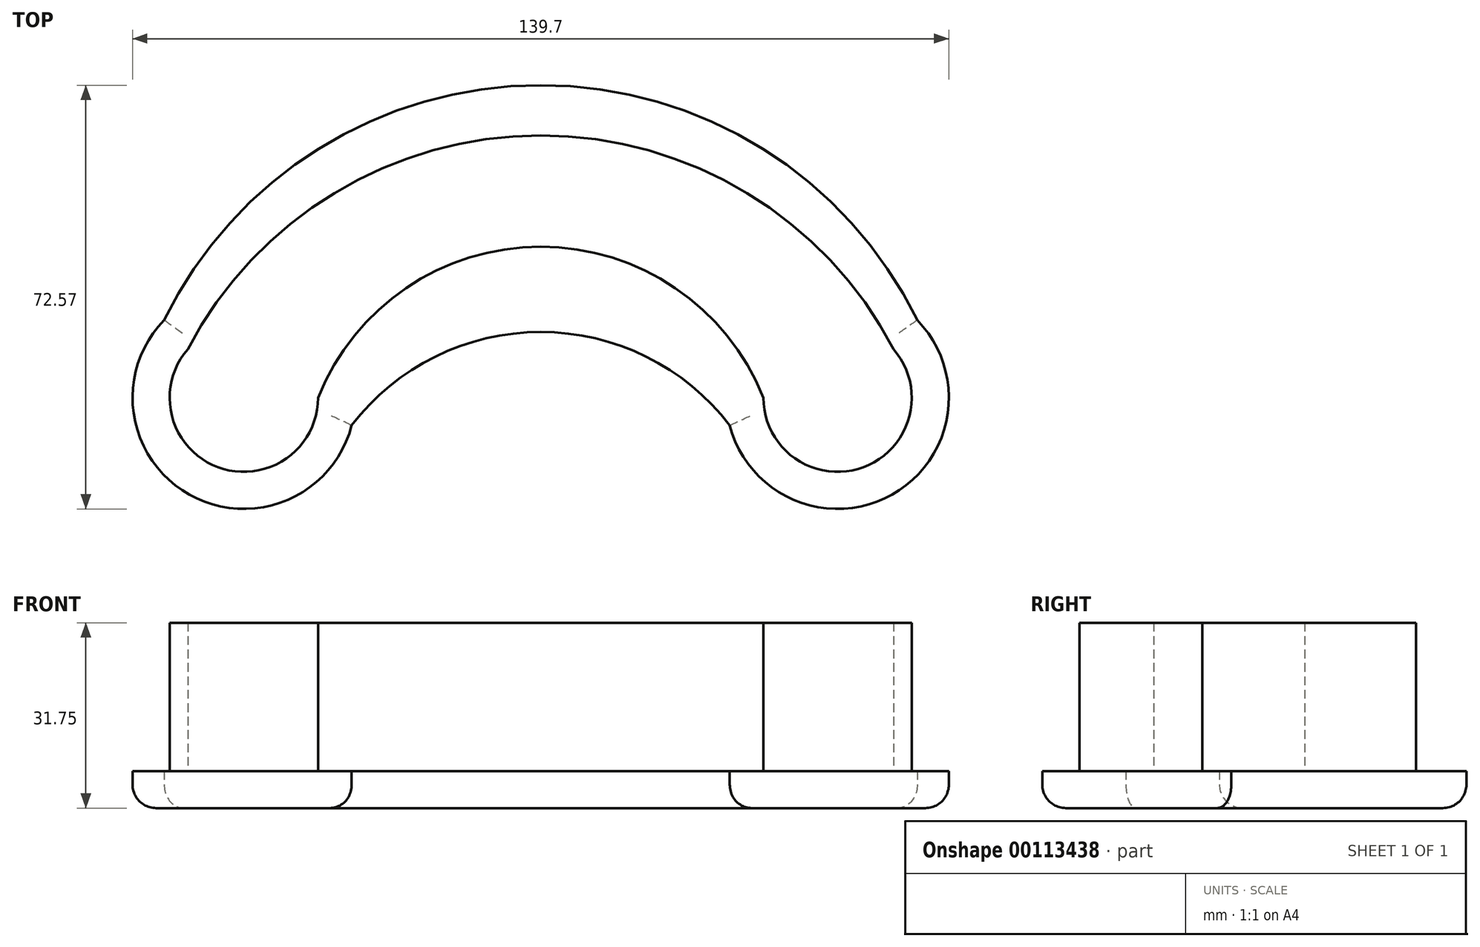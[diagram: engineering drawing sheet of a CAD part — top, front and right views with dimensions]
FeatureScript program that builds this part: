
annotation { "Feature Type Name" : "Feature", "Feature Type Description" : "" }
export const myFeature = defineFeature(function(context is Context, id is Id, definition is map)
    precondition{}
    {
        {
            var Q0;
            Q0=qCreatedBy(makeId("Top.planeOp"),FACE);
            var sketch = newSketch(context, id + "F0", { "sketchPlane" : qUnion([Q0])});
            skCircle(sketch, "E0", {"center": v(-44.09, 19.27) * mm, "radius": 19.05 * mm});
            skCircle(sketch, "E1", {"center": v(57.51, 19.27) * mm, "radius": 19.05 * mm});
            skLineSegment(sketch, "E2", {"start": v(-44.09, 19.27) * mm, "end": v(57.51, 19.27) * mm});
            skLineSegment(sketch, "E3", {"start": v(-57.73, 32.57) * mm, "end": v(71.15, 32.57) * mm});
            skLineSegment(sketch, "E4", {"start": v(-25.64, 14.52) * mm, "end": v(39.06, 14.52) * mm});
            skArc(sketch, "E5", {"start": v(71.15, 32.57) * mm, "mid": v(6.71, 72.8) * mm, "end": v(-57.73, 32.57) * mm});
            skArc(sketch, "E6", {"start": v(39.06, 14.52) * mm, "mid": v(6.71, 30.53) * mm, "end": v(-25.64, 14.52) * mm});
            skSolve(sketch);
        }
        {
            var Q0;
            {var subQ0=sQuery(id+"F0.wireOp",EDGE,"E0");var subQ1=makeQuery(id+"F0.imprint","INTERSECT",VERTEX,{"derivedFrom":[subQ0,sQuery(id+"F0.wireOp",EDGE,"E2")]});Q0=makeQuery(id+"F0.imprint","IMPRINT",FACE,{"disambiguationData":[TD([[makeQuery(id+"F0.imprint","IMPRINT",EDGE,{"disambiguationData":[TD([[subQ1,-1.0]])],"derivedFrom":subQ0}),1.0]])]});}
            var Q1;
            {var subQ0=sQuery(id+"F0.wireOp",EDGE,"cqztKuuP-2mC5-SIxx-0093-MniZhsKi1Iyt");var subQ1=sQuery(id+"F0.wireOp",EDGE,"E0");var subQ2=makeQuery(id+"F0.imprint","INTERSECT",VERTEX,{"derivedFrom":[subQ1,subQ0]});Q1=makeQuery(id+"F0.imprint","IMPRINT",FACE,{"disambiguationData":[TD([[makeQuery(id+"F0.imprint","IMPRINT",EDGE,{"disambiguationData":[TD([[subQ2,1.0]])],"derivedFrom":subQ1}),1.0]])]});}
            var Q2;
            {var subQ0=sQuery(id+"F0.wireOp",EDGE,"cqztKuuP-2mC5-SIxx-0093-MniZhsKi1Iyt");var subQ1=sQuery(id+"F0.wireOp",EDGE,"E0");var subQ2=makeQuery(id+"F0.imprint","INTERSECT",VERTEX,{"derivedFrom":[subQ1,subQ0]});Q2=makeQuery(id+"F0.imprint","IMPRINT",FACE,{"disambiguationData":[TD([[makeQuery(id+"F0.imprint","IMPRINT",EDGE,{"disambiguationData":[TD([[subQ2,1.0]])],"derivedFrom":subQ1}),-1.0]])]});}
            var Q3;
            {var subQ0=sQuery(id+"F0.wireOp",EDGE,"cqztKuuP-2mC5-SIxx-0093-MniZhsKi1Iyt");var subQ1=sQuery(id+"F0.wireOp",EDGE,"E1");var subQ2=makeQuery(id+"F0.imprint","INTERSECT",VERTEX,{"derivedFrom":[subQ1,subQ0]});Q3=makeQuery(id+"F0.imprint","IMPRINT",FACE,{"disambiguationData":[TD([[makeQuery(id+"F0.imprint","IMPRINT",EDGE,{"disambiguationData":[TD([[subQ2,-1.0]])],"derivedFrom":subQ1}),1.0]])]});}
            var Q4;
            {var subQ0=sQuery(id+"F0.wireOp",EDGE,"E1");var subQ1=makeQuery(id+"F0.imprint","INTERSECT",VERTEX,{"derivedFrom":[subQ0,sQuery(id+"F0.wireOp",EDGE,"E2")]});Q4=makeQuery(id+"F0.imprint","IMPRINT",FACE,{"disambiguationData":[TD([[makeQuery(id+"F0.imprint","IMPRINT",EDGE,{"disambiguationData":[TD([[subQ1,1.0]])],"derivedFrom":subQ0}),1.0]])]});}
            var Q5;
            {var subQ1=sQuery(id+"F0.wireOp",EDGE,"E1");var subQ3=sQuery(id+"F0.wireOp",EDGE,"E2");var subQ4=makeQuery(id+"F0.imprint","INTERSECT",VERTEX,{"derivedFrom":[subQ1,subQ3]});Q5=makeQuery(id+"F0.imprint","IMPRINT",FACE,{"disambiguationData":[TD([[makeQuery(id+"F0.imprint","IMPRINT",EDGE,{"disambiguationData":[TD([[subQ4,1.0]])],"derivedFrom":subQ3}),-1.0]])]});}
            var Q6;
            {var subQ1=sQuery(id+"F0.wireOp",EDGE,"E0");var subQ3=sQuery(id+"F0.wireOp",EDGE,"E2");var subQ4=makeQuery(id+"F0.imprint","INTERSECT",VERTEX,{"derivedFrom":[subQ1,subQ3]});Q6=makeQuery(id+"F0.imprint","IMPRINT",FACE,{"disambiguationData":[TD([[makeQuery(id+"F0.imprint","IMPRINT",EDGE,{"disambiguationData":[TD([[subQ4,-1.0]])],"derivedFrom":subQ3}),-1.0]])]});}
            var Q7;
            {var subQ0=sQuery(id+"F0.wireOp",EDGE,"jA0AjXC6-elOE-Hy4x-EZsK-m11m4aKZ461u");var subQ1=sQuery(id+"F0.wireOp",EDGE,"E0");var subQ2=makeQuery(id+"F0.imprint","INTERSECT",VERTEX,{"derivedFrom":[subQ1,subQ0]});Q7=makeQuery(id+"F0.imprint","IMPRINT",FACE,{"disambiguationData":[TD([[makeQuery(id+"F0.imprint","IMPRINT",EDGE,{"disambiguationData":[TD([[subQ2,1.0]])],"derivedFrom":subQ1}),-1.0]])]});}
            var Q8;
            {var subQ0=sQuery(id+"F0.wireOp",EDGE,"jA0AjXC6-elOE-Hy4x-EZsK-m11m4aKZ461u");var subQ1=sQuery(id+"F0.wireOp",EDGE,"E0");var subQ2=makeQuery(id+"F0.imprint","INTERSECT",VERTEX,{"derivedFrom":[subQ1,subQ0]});Q8=makeQuery(id+"F0.imprint","IMPRINT",FACE,{"disambiguationData":[TD([[makeQuery(id+"F0.imprint","IMPRINT",EDGE,{"disambiguationData":[TD([[subQ2,1.0]])],"derivedFrom":subQ1}),1.0]])]});}
            var Q9;
            {var subQ0=sQuery(id+"F0.wireOp",EDGE,"jA0AjXC6-elOE-Hy4x-EZsK-m11m4aKZ461u");var subQ1=sQuery(id+"F0.wireOp",EDGE,"E1");var subQ2=makeQuery(id+"F0.imprint","INTERSECT",VERTEX,{"derivedFrom":[subQ1,subQ0]});Q9=makeQuery(id+"F0.imprint","IMPRINT",FACE,{"disambiguationData":[TD([[makeQuery(id+"F0.imprint","IMPRINT",EDGE,{"disambiguationData":[TD([[subQ2,-1.0]])],"derivedFrom":subQ1}),1.0]])]});}
            var Q10;
            {var subQ0=sQuery(id+"F0.wireOp",EDGE,"E5");Q10=makeQuery(id+"F0.imprint","IMPRINT",FACE,{"disambiguationData":[TD([[makeQuery(id+"F0.imprint","IMPRINT",EDGE,{"derivedFrom":subQ0}),1.0]])]});}
            var Q11;
            {var subQ0=sQuery(id+"F0.wireOp",EDGE,"E3");var subQ1=sQuery(id+"F0.wireOp",EDGE,"E1");var subQ3=makeQuery(id+"F0.imprint","INTERSECT",VERTEX,{"derivedFrom":[subQ1,subQ0]});Q11=makeQuery(id+"F0.imprint","IMPRINT",FACE,{"disambiguationData":[TD([[makeQuery(id+"F0.imprint","IMPRINT",EDGE,{"disambiguationData":[TD([[subQ3,1.0]])],"derivedFrom":subQ1}),1.0]])]});}
            var Q12;
            {var subQ0=sQuery(id+"F0.wireOp",EDGE,"E3");var subQ1=sQuery(id+"F0.wireOp",EDGE,"E0");var subQ3=makeQuery(id+"F0.imprint","INTERSECT",VERTEX,{"derivedFrom":[subQ1,subQ0]});Q12=makeQuery(id+"F0.imprint","IMPRINT",FACE,{"disambiguationData":[TD([[makeQuery(id+"F0.imprint","IMPRINT",EDGE,{"disambiguationData":[TD([[subQ3,-1.0]])],"derivedFrom":subQ1}),1.0]])]});}
            var Q13;
            {var subQ0=sQuery(id+"F0.wireOp",EDGE,"E2");var subQ5=sQuery(id+"F0.wireOp",EDGE,"E0");var subQ6=makeQuery(id+"F0.imprint","INTERSECT",VERTEX,{"derivedFrom":[subQ5,subQ0]});Q13=makeQuery(id+"F0.imprint","IMPRINT",FACE,{"disambiguationData":[TD([[makeQuery(id+"F0.imprint","IMPRINT",EDGE,{"disambiguationData":[TD([[subQ6,-1.0]])],"derivedFrom":subQ5}),-1.0]])]});}
            extrude(context, id + "F1", {"entities" : qUnion([Q0, Q1, Q2, Q3, Q4, Q5, Q6, Q7, Q8, Q9, Q10, Q11, Q12, Q13]), "depth" : 6.35 * mm});
        }
        {
            var Q0;
            Q0=makeQuery(id+"F1.opExtrude","CAP_FACE",FACE,{"disambiguationData":[OSD([sQuery(id+"F0.wireOp",EDGE,"E0"),sQuery(id+"F0.wireOp",EDGE,"E1"),sQuery(id+"F0.wireOp",EDGE,"OMICP9Pv-Sj9Z-tNpq-0osr-h563eNZeSqYc"),sQuery(id+"F0.wireOp",EDGE,"jA0AjXC6-elOE-Hy4x-EZsK-m11m4aKZ461u")])],"isStart":false});
            var sketch = newSketch(context, id + "F2", { "sketchPlane" : qUnion([Q0])});
            skCircle(sketch, "E7", {"center": v(-44.09, 19.27) * mm, "radius": 12.7 * mm});
            skCircle(sketch, "E8", {"center": v(57.51, 19.27) * mm, "radius": 12.7 * mm});
            skLineSegment(sketch, "E9", {"start": v(-53.7, 27.58) * mm, "end": v(67.12, 27.58) * mm});
            skArc(sketch, "E10", {"start": v(44.81, 19.27) * mm, "mid": v(6.71, 45.13) * mm, "end": v(-31.39, 19.27) * mm});
            skArc(sketch, "E11", {"start": v(67.12, 27.58) * mm, "mid": v(6.71, 64.19) * mm, "end": v(-53.7, 27.58) * mm});
            skSolve(sketch);
        }
        {
            var Q0;
            {var subQ0=sQuery(id+"F2.wireOp",EDGE,"E7");var subQ1=makeQuery(id+"F2.imprint","INTERSECT",VERTEX,{"derivedFrom":[subQ0,sQuery(id+"F2.wireOp",EDGE,"E10")]});Q0=makeQuery(id+"F2.imprint","IMPRINT",FACE,{"disambiguationData":[TD([[makeQuery(id+"F2.imprint","IMPRINT",EDGE,{"disambiguationData":[TD([[subQ1,-1.0]])],"derivedFrom":subQ0}),1.0]])]});}
            var Q1;
            {var subQ0=sQuery(id+"F2.wireOp",EDGE,"E9");var subQ1=sQuery(id+"F2.wireOp",EDGE,"E7");var subQ3=makeQuery(id+"F2.imprint","INTERSECT",VERTEX,{"derivedFrom":[subQ1,subQ0]});Q1=makeQuery(id+"F2.imprint","IMPRINT",FACE,{"disambiguationData":[TD([[makeQuery(id+"F2.imprint","IMPRINT",EDGE,{"disambiguationData":[TD([[subQ3,-1.0]])],"derivedFrom":subQ1}),1.0]])]});}
            var Q2;
            {var subQ8=sQuery(id+"F2.wireOp",EDGE,"E11");Q2=makeQuery(id+"F2.imprint","IMPRINT",FACE,{"disambiguationData":[TD([[makeQuery(id+"F2.imprint","IMPRINT",EDGE,{"derivedFrom":subQ8}),1.0]])]});}
            var Q3;
            {var subQ0=sQuery(id+"F2.wireOp",EDGE,"E9");var subQ1=sQuery(id+"F2.wireOp",EDGE,"E8");var subQ3=makeQuery(id+"F2.imprint","INTERSECT",VERTEX,{"derivedFrom":[subQ1,subQ0]});Q3=makeQuery(id+"F2.imprint","IMPRINT",FACE,{"disambiguationData":[TD([[makeQuery(id+"F2.imprint","IMPRINT",EDGE,{"disambiguationData":[TD([[subQ3,1.0]])],"derivedFrom":subQ1}),1.0]])]});}
            var Q4;
            {var subQ0=sQuery(id+"F2.wireOp",EDGE,"E8");var subQ1=makeQuery(id+"F2.imprint","INTERSECT",VERTEX,{"derivedFrom":[subQ0,sQuery(id+"F2.wireOp",EDGE,"E10")]});Q4=makeQuery(id+"F2.imprint","IMPRINT",FACE,{"disambiguationData":[TD([[makeQuery(id+"F2.imprint","IMPRINT",EDGE,{"disambiguationData":[TD([[subQ1,1.0]])],"derivedFrom":subQ0}),1.0]])]});}
            var Q5;
            {var subQ0=sQuery(id+"F2.wireOp",EDGE,"E10");var subQ1=sQuery(id+"F2.wireOp",EDGE,"E8");var subQ2=makeQuery(id+"F2.imprint","INTERSECT",VERTEX,{"derivedFrom":[subQ1,subQ0]});Q5=makeQuery(id+"F2.imprint","IMPRINT",FACE,{"disambiguationData":[TD([[makeQuery(id+"F2.imprint","IMPRINT",EDGE,{"disambiguationData":[TD([[subQ2,1.0]])],"derivedFrom":subQ1}),-1.0]])]});}
            var Q6;
            {var subQ0=sQuery(id+"F2.wireOp",EDGE,"E10");var subQ1=sQuery(id+"F2.wireOp",EDGE,"E7");var subQ2=makeQuery(id+"F2.imprint","INTERSECT",VERTEX,{"derivedFrom":[subQ1,subQ0]});Q6=makeQuery(id+"F2.imprint","IMPRINT",FACE,{"disambiguationData":[TD([[makeQuery(id+"F2.imprint","IMPRINT",EDGE,{"disambiguationData":[TD([[subQ2,-1.0]])],"derivedFrom":subQ1}),-1.0]])]});}
            extrude(context, id + "F3", {"entities" : qUnion([Q0, Q1, Q2, Q3, Q4, Q5, Q6]), "operationType" : NewBodyOperationType.ADD, "depth" : 25.4 * mm});
        }
        {
            var Q0;
            Q0=makeQuery(id+"F1.opExtrude","CAP_FACE",FACE,{"disambiguationData":[OSD([sQuery(id+"F0.wireOp",EDGE,"E0"),sQuery(id+"F0.wireOp",EDGE,"E1"),sQuery(id+"F0.wireOp",EDGE,"OMICP9Pv-Sj9Z-tNpq-0osr-h563eNZeSqYc"),sQuery(id+"F0.wireOp",EDGE,"jA0AjXC6-elOE-Hy4x-EZsK-m11m4aKZ461u")])],"isStart":true});
            fillet(context, id + "F4", {"entities" : qUnion([Q0]), "radius" : 4.02 * mm, "tangentPropagation" : true, "allowEdgeOverflow" : false});
        }
    });
